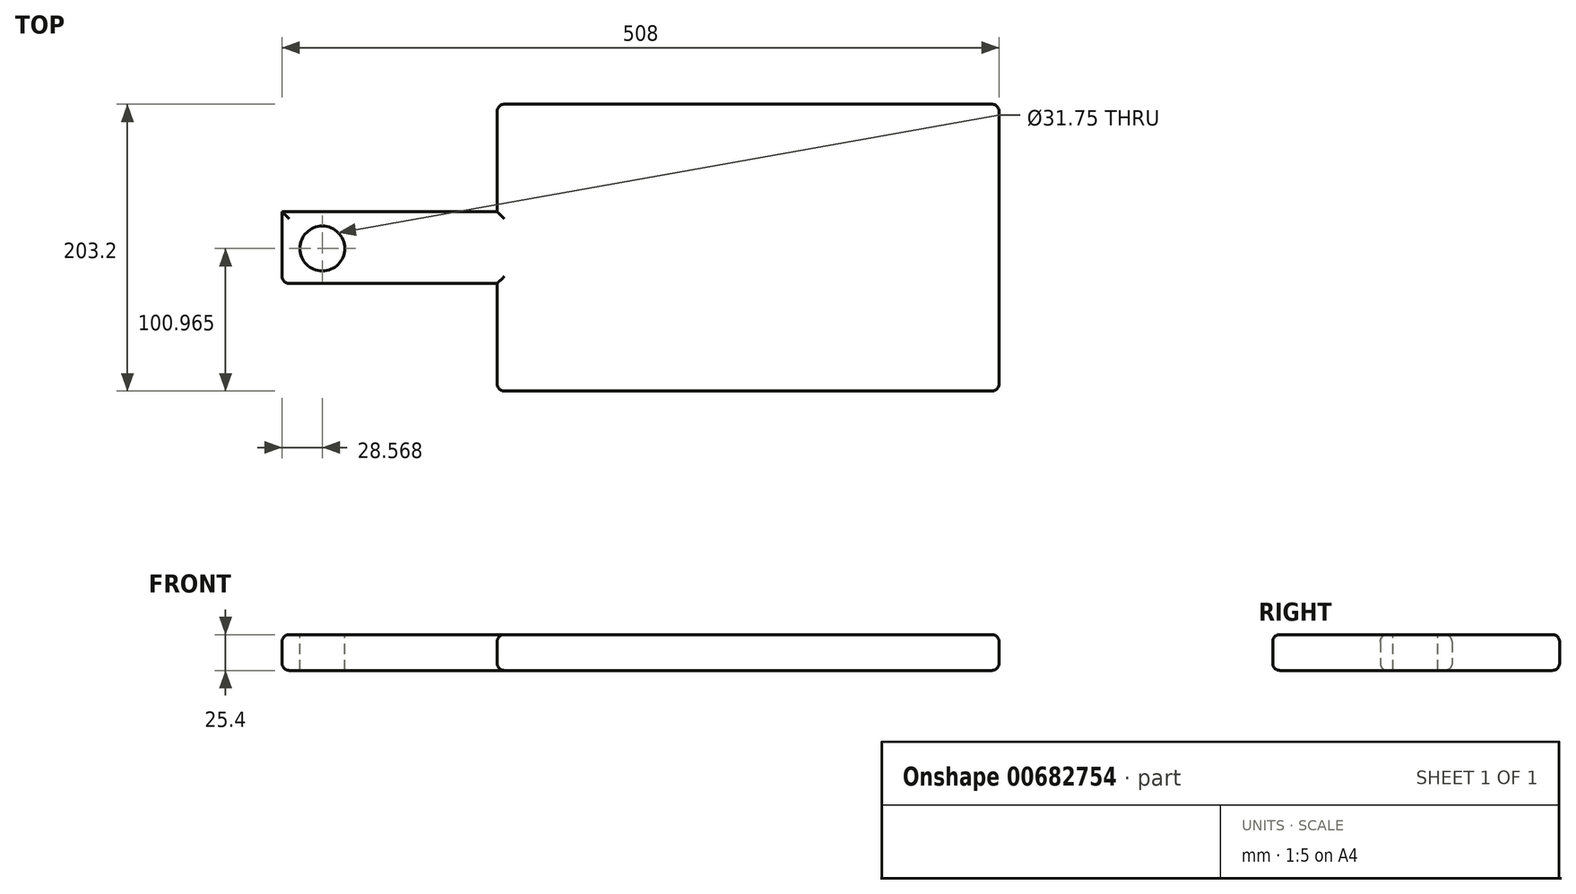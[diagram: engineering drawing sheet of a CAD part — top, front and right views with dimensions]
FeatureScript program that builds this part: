
annotation { "Feature Type Name" : "Feature", "Feature Type Description" : "" }
export const myFeature = defineFeature(function(context is Context, id is Id, definition is map)
    precondition{}
    {
        {
            var Q0;
            Q0=qCreatedBy(makeId("Top.planeOp"),FACE);
            var sketch = newSketch(context, id + "F0", { "sketchPlane" : qUnion([Q0])});
            skLineSegment(sketch, "E0.bottom", {"start": v(0, 0) * mm, "end": v(355.6, 0) * mm});
            skLineSegment(sketch, "E0.top", {"start": v(0, 203.2) * mm, "end": v(355.6, 203.2) * mm});
            skLineSegment(sketch, "E0.left", {"start": v(0, 0) * mm, "end": v(0, 203.2) * mm});
            skLineSegment(sketch, "E0.right", {"start": v(355.6, 0) * mm, "end": v(355.6, 203.2) * mm});
            skLineSegment(sketch, "E1.bottom", {"start": v(0, 127) * mm, "end": v(-152.4, 127) * mm});
            skLineSegment(sketch, "E1.top", {"start": v(0, 76.2) * mm, "end": v(-152.4, 76.2) * mm});
            skLineSegment(sketch, "E1.left", {"start": v(0, 127) * mm, "end": v(0, 76.2) * mm});
            skLineSegment(sketch, "E1.right", {"start": v(-152.4, 127) * mm, "end": v(-152.4, 76.2) * mm});
            skSolve(sketch);
        }
        {
            var Q0;
            {var subQ3=sQuery(id+"F0.wireOp",EDGE,"E0.bottom");Q0=makeQuery(id+"F0.imprint","IMPRINT",FACE,{"disambiguationData":[TD([[makeQuery(id+"F0.imprint","IMPRINT",EDGE,{"derivedFrom":subQ3}),1.0]])]});}
            var Q1;
            Q1=makeQuery(id+"F0.imprint","IMPRINT",FACE,{"disambiguationData":[TD([[makeQuery(id+"F0.imprint","IMPRINT",EDGE,{"derivedFrom":sQuery(id+"F0.wireOp",EDGE,"E1.bottom")}),1.0]])]});
            extrude(context, id + "F1", {"entities" : qUnion([Q0, Q1]), "depth" : 25.4 * mm, "offsetDistance" : 25.4 * mm});
        }
        {
            var Q0;
            Q0=makeQuery(id+"F1.opExtrude","CAP_FACE",FACE,{"disambiguationData":[OSD([sQuery(id+"F0.wireOp",EDGE,"E0.bottom"),sQuery(id+"F0.wireOp",EDGE,"E0.top"),sQuery(id+"F0.wireOp",EDGE,"E0.left"),sQuery(id+"F0.wireOp",EDGE,"E0.right"),sQuery(id+"F0.wireOp",EDGE,"E1.bottom"),sQuery(id+"F0.wireOp",EDGE,"E1.top"),sQuery(id+"F0.wireOp",EDGE,"E1.right")])],"isStart":false});
            var sketch = newSketch(context, id + "F2", { "sketchPlane" : qUnion([Q0])});
            skCircle(sketch, "E2", {"center": v(-123.83, 100.97) * mm, "radius": 15.88 * mm});
            skSolve(sketch);
        }
        {
            var Q0;
            Q0=makeQuery(id+"F2.imprint","IMPRINT",FACE,{"disambiguationData":[TD([[makeQuery(id+"F2.imprint","IMPRINT",EDGE,{"derivedFrom":sQuery(id+"F2.wireOp",EDGE,"E2")}),-1.0]])]});
            var sketch = newSketch(context, id + "F3", { "sketchPlane" : qUnion([Q0])});
            skSolve(sketch);
        }
        {
            var Q0;
            Q0=makeQuery(id+"F2.imprint","IMPRINT",FACE,{"disambiguationData":[TD([[makeQuery(id+"F2.imprint","IMPRINT",EDGE,{"derivedFrom":sQuery(id+"F2.wireOp",EDGE,"E2")}),1.0]])]});
            extrude(context, id + "F4", {"entities" : qUnion([Q0]), "operationType" : NewBodyOperationType.REMOVE, "endBound" : BoundingType.THROUGH_ALL, "oppositeDirection" : true, "depth" : 25.4 * mm, "offsetDistance" : 25.4 * mm});
        }
        {
            var Q0;
            Q0=makeQuery(id+"F1.opExtrude","SWEPT_EDGE",EDGE,{"disambiguationData":[OSD([sQuery(id+"F0.wireOp",EDGE,"E1.top"),sQuery(id+"F0.wireOp",EDGE,"E1.right")])]});
            var Q1;
            Q1=makeQuery(id+"F1.opExtrude","CAP_EDGE",EDGE,{"disambiguationData":[OSD([sQuery(id+"F0.wireOp",EDGE,"E1.bottom")])],"isStart":false});
            var Q2;
            Q2=makeQuery(id+"F1.opExtrude","CAP_EDGE",EDGE,{"disambiguationData":[OSD([sQuery(id+"F0.wireOp",EDGE,"E1.right")])],"isStart":false});
            var Q3;
            Q3=makeQuery(id+"F1.opExtrude","CAP_EDGE",EDGE,{"disambiguationData":[OSD([sQuery(id+"F0.wireOp",EDGE,"E1.top")])],"isStart":false});
            var Q4;
            Q4=makeQuery(id+"F1.opExtrude","CAP_EDGE",EDGE,{"disambiguationData":[OSD([sQuery(id+"F0.wireOp",EDGE,"E1.top")])],"isStart":true});
            var Q5;
            {var subQ0=sQuery(id+"F0.wireOp",EDGE,"E0.left");Q5=makeQuery(id+"F1.opExtrude","CAP_EDGE",EDGE,{"disambiguationData":[OSD([subQ0]),TDD([makeQuery(id+"F0.imprint","IMPRINT",EDGE,{"disambiguationData":[TD([[makeQuery(id+"F0.imprint","INTERSECT",VERTEX,{"derivedFrom":[sQuery(id+"F0.wireOp",EDGE,"E0.bottom"),subQ0]}),-1.0]])],"derivedFrom":subQ0})])],"isStart":false});}
            var Q6;
            {var subQ0=sQuery(id+"F0.wireOp",EDGE,"E0.left");Q6=makeQuery(id+"F1.opExtrude","CAP_EDGE",EDGE,{"disambiguationData":[OSD([subQ0]),TDD([makeQuery(id+"F0.imprint","IMPRINT",EDGE,{"disambiguationData":[TD([[makeQuery(id+"F0.imprint","INTERSECT",VERTEX,{"derivedFrom":[sQuery(id+"F0.wireOp",EDGE,"E0.top"),subQ0]}),1.0]])],"derivedFrom":subQ0})])],"isStart":false});}
            var Q7;
            Q7=makeQuery(id+"F1.opExtrude","CAP_EDGE",EDGE,{"disambiguationData":[OSD([sQuery(id+"F0.wireOp",EDGE,"E0.top")])],"isStart":false});
            var Q8;
            Q8=makeQuery(id+"F1.opExtrude","CAP_EDGE",EDGE,{"disambiguationData":[OSD([sQuery(id+"F0.wireOp",EDGE,"E0.bottom")])],"isStart":false});
            var Q9;
            Q9=makeQuery(id+"F1.opExtrude","CAP_EDGE",EDGE,{"disambiguationData":[OSD([sQuery(id+"F0.wireOp",EDGE,"E0.bottom")])],"isStart":true});
            var Q10;
            Q10=makeQuery(id+"F1.opExtrude","SWEPT_EDGE",EDGE,{"disambiguationData":[OSD([sQuery(id+"F0.wireOp",EDGE,"E0.bottom"),sQuery(id+"F0.wireOp",EDGE,"E0.left")])]});
            var Q11;
            Q11=makeQuery(id+"F1.opExtrude","CAP_EDGE",EDGE,{"disambiguationData":[OSD([sQuery(id+"F0.wireOp",EDGE,"E0.right")])],"isStart":false});
            var Q12;
            Q12=makeQuery(id+"F1.opExtrude","SWEPT_EDGE",EDGE,{"disambiguationData":[OSD([sQuery(id+"F0.wireOp",EDGE,"E0.bottom"),sQuery(id+"F0.wireOp",EDGE,"E0.right")])]});
            var Q13;
            Q13=makeQuery(id+"F1.opExtrude","CAP_EDGE",EDGE,{"disambiguationData":[OSD([sQuery(id+"F0.wireOp",EDGE,"E0.right")])],"isStart":true});
            var Q14;
            Q14=makeQuery(id+"F1.opExtrude","SWEPT_EDGE",EDGE,{"disambiguationData":[OSD([sQuery(id+"F0.wireOp",EDGE,"E0.top"),sQuery(id+"F0.wireOp",EDGE,"E0.right")])]});
            var Q15;
            Q15=makeQuery(id+"F1.opExtrude","CAP_EDGE",EDGE,{"disambiguationData":[OSD([sQuery(id+"F0.wireOp",EDGE,"E0.top")])],"isStart":true});
            var Q16;
            {var subQ0=sQuery(id+"F0.wireOp",EDGE,"E0.left");Q16=makeQuery(id+"F1.opExtrude","CAP_EDGE",EDGE,{"disambiguationData":[OSD([subQ0]),TDD([makeQuery(id+"F0.imprint","IMPRINT",EDGE,{"disambiguationData":[TD([[makeQuery(id+"F0.imprint","INTERSECT",VERTEX,{"derivedFrom":[sQuery(id+"F0.wireOp",EDGE,"E0.bottom"),subQ0]}),-1.0]])],"derivedFrom":subQ0})])],"isStart":true});}
            var Q17;
            {var subQ0=sQuery(id+"F0.wireOp",EDGE,"E0.left");Q17=makeQuery(id+"F1.opExtrude","CAP_EDGE",EDGE,{"disambiguationData":[OSD([subQ0]),TDD([makeQuery(id+"F0.imprint","IMPRINT",EDGE,{"disambiguationData":[TD([[makeQuery(id+"F0.imprint","INTERSECT",VERTEX,{"derivedFrom":[sQuery(id+"F0.wireOp",EDGE,"E0.top"),subQ0]}),1.0]])],"derivedFrom":subQ0})])],"isStart":true});}
            var Q18;
            Q18=makeQuery(id+"F1.opExtrude","SWEPT_EDGE",EDGE,{"disambiguationData":[OSD([sQuery(id+"F0.wireOp",EDGE,"E0.top"),sQuery(id+"F0.wireOp",EDGE,"E0.left")])]});
            var Q19;
            Q19=makeQuery(id+"F1.opExtrude","CAP_EDGE",EDGE,{"disambiguationData":[OSD([sQuery(id+"F0.wireOp",EDGE,"E1.right")])],"isStart":true});
            var Q20;
            Q20=makeQuery(id+"F1.opExtrude","CAP_EDGE",EDGE,{"disambiguationData":[OSD([sQuery(id+"F0.wireOp",EDGE,"E1.bottom")])],"isStart":true});
            fillet(context, id + "F5", {"entities" : qUnion([Q0, Q1, Q2, Q3, Q4, Q5, Q6, Q7, Q8, Q9, Q10, Q11, Q12, Q13, Q14, Q15, Q16, Q17, Q18, Q19, Q20]), "radius" : 5.08 * mm, "tangentPropagation" : true, "allowEdgeOverflow" : false});
        }
    });
